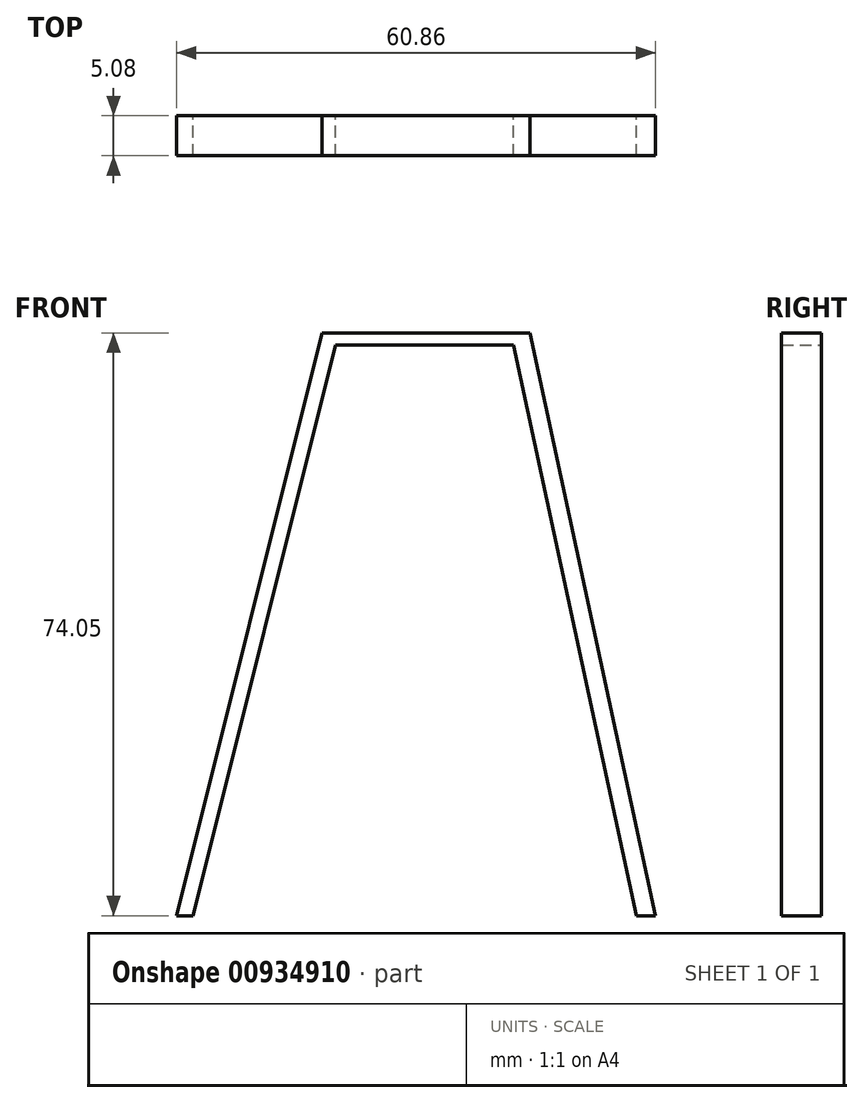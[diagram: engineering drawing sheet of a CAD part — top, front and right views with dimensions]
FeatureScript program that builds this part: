
annotation { "Feature Type Name" : "Feature", "Feature Type Description" : "" }
export const myFeature = defineFeature(function(context is Context, id is Id, definition is map)
    precondition{}
    {
        {
            var Q0;
            Q0=qCreatedBy(makeId("Front.planeOp"),FACE);
            var sketch = newSketch(context, id + "F0", { "sketchPlane" : qUnion([Q0])});
            skLineSegment(sketch, "E0", {"start": v(-51.52, 0) * mm, "end": v(-33.07, 74.05) * mm});
            skLineSegment(sketch, "E1", {"start": v(-33.07, 74.05) * mm, "end": v(-6.63, 74.05) * mm});
            skLineSegment(sketch, "E2", {"start": v(-6.63, 74.05) * mm, "end": v(9.34, 0) * mm});
            skLineSegment(sketch, "E3", {"start": v(9.34, 0) * mm, "end": v(6.9, 0) * mm});
            skLineSegment(sketch, "E4", {"start": v(6.9, 0) * mm, "end": v(-8.72, 72.48) * mm});
            skLineSegment(sketch, "E5", {"start": v(-8.72, 72.48) * mm, "end": v(-31.32, 72.48) * mm});
            skLineSegment(sketch, "E6", {"start": v(-31.32, 72.48) * mm, "end": v(-49.4, 0) * mm});
            skLineSegment(sketch, "E7", {"start": v(-49.4, 0) * mm, "end": v(-51.52, 0) * mm});
            skSolve(sketch);
        }
        {
            var Q0;
            Q0=makeQuery(id+"F0.imprint","IMPRINT",FACE,{"disambiguationData":[TD([[makeQuery(id+"F0.imprint","IMPRINT",EDGE,{"derivedFrom":sQuery(id+"F0.wireOp",EDGE,"E0")}),-1.0]])]});
            extrude(context, id + "F1", {"entities" : qUnion([Q0]), "depth" : 5.08 * mm, "offsetDistance" : 25.4 * mm});
        }
    });
